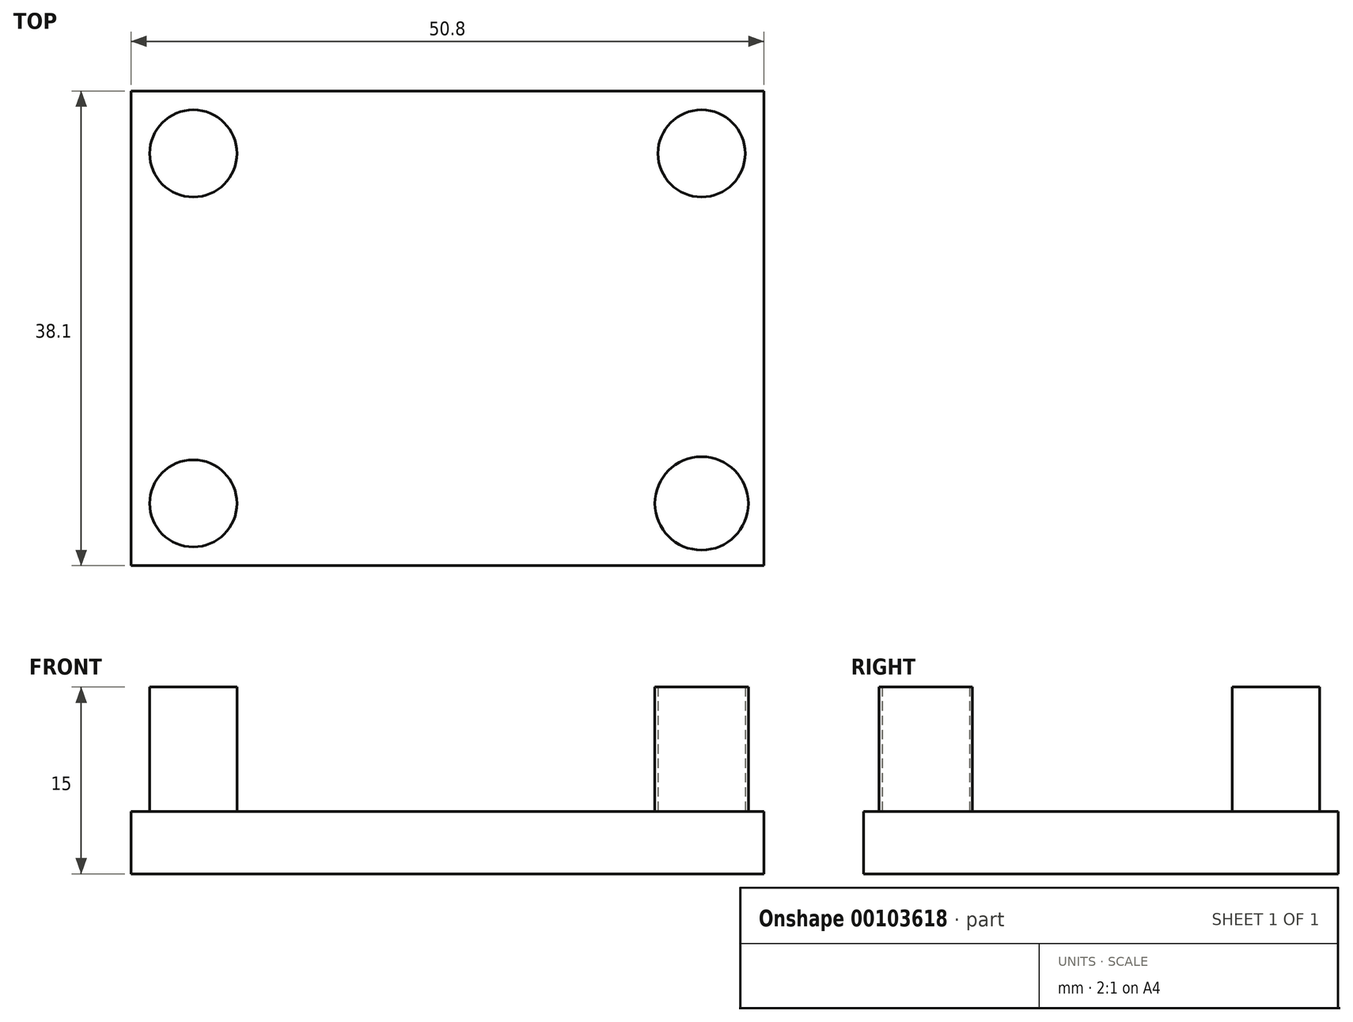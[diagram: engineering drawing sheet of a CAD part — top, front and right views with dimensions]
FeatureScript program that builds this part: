
annotation { "Feature Type Name" : "Feature", "Feature Type Description" : "" }
export const myFeature = defineFeature(function(context is Context, id is Id, definition is map)
    precondition{}
    {
        {
            var Q0;
            Q0=qCreatedBy(makeId("Top.planeOp"),FACE);
            var sketch = newSketch(context, id + "F0", { "sketchPlane" : qUnion([Q0])});
            skLineSegment(sketch, "E0.bottom", {"start": v(-32.92, 10.92) * mm, "end": v(17.88, 10.92) * mm});
            skLineSegment(sketch, "E0.top", {"start": v(-32.92, -27.18) * mm, "end": v(17.88, -27.18) * mm});
            skLineSegment(sketch, "E0.left", {"start": v(-32.92, 10.92) * mm, "end": v(-32.92, -27.18) * mm});
            skLineSegment(sketch, "E0.right", {"start": v(17.88, 10.92) * mm, "end": v(17.88, -27.18) * mm});
            skSolve(sketch);
        }
        {
            var Q0;
            Q0=makeQuery(id+"F0.imprint","IMPRINT",FACE,{"disambiguationData":[TD([[makeQuery(id+"F0.imprint","IMPRINT",EDGE,{"derivedFrom":sQuery(id+"F0.wireOp",EDGE,"E0.bottom")}),-1.0]])]});
            extrude(context, id + "F1", {"entities" : qUnion([Q0]), "depth" : 5 * mm});
        }
        {
            var Q0;
            Q0=makeQuery(id+"F1.opExtrude","CAP_FACE",FACE,{"disambiguationData":[OSD([sQuery(id+"F0.wireOp",EDGE,"E0.bottom"),sQuery(id+"F0.wireOp",EDGE,"E0.top"),sQuery(id+"F0.wireOp",EDGE,"E0.left"),sQuery(id+"F0.wireOp",EDGE,"E0.right")])],"isStart":false});
            var sketch = newSketch(context, id + "F2", { "sketchPlane" : qUnion([Q0])});
            skPoint(sketch, "E1", {"position": v(-27.92, -22.18) * mm});
            skCircle(sketch, "E2", {"center": v(-27.92, -22.18) * mm, "radius": 3.5 * mm});
            skPoint(sketch, "E3", {"position": v(-27.92, 5.92) * mm});
            skCircle(sketch, "E4", {"center": v(-27.92, 5.92) * mm, "radius": 3.5 * mm});
            skPoint(sketch, "E5", {"position": v(12.88, 5.92) * mm});
            skCircle(sketch, "E6", {"center": v(12.88, 5.92) * mm, "radius": 3.5 * mm});
            skPoint(sketch, "E7", {"position": v(12.88, -22.18) * mm});
            skCircle(sketch, "E8", {"center": v(12.88, -22.18) * mm, "radius": 3.75 * mm});
            skSolve(sketch);
        }
        {
            var Q0;
            Q0=makeQuery(id+"F2.imprint","IMPRINT",FACE,{"disambiguationData":[TD([[makeQuery(id+"F2.imprint","IMPRINT",EDGE,{"derivedFrom":sQuery(id+"F2.wireOp",EDGE,"E2")}),1.0]])]});
            var Q1;
            Q1=makeQuery(id+"F2.imprint","IMPRINT",FACE,{"disambiguationData":[TD([[makeQuery(id+"F2.imprint","IMPRINT",EDGE,{"derivedFrom":sQuery(id+"F2.wireOp",EDGE,"E6")}),1.0]])]});
            var Q2;
            Q2=makeQuery(id+"F2.imprint","IMPRINT",FACE,{"disambiguationData":[TD([[makeQuery(id+"F2.imprint","IMPRINT",EDGE,{"derivedFrom":sQuery(id+"F2.wireOp",EDGE,"E8")}),1.0]])]});
            var Q3;
            Q3=makeQuery(id+"F2.imprint","IMPRINT",FACE,{"disambiguationData":[TD([[makeQuery(id+"F2.imprint","IMPRINT",EDGE,{"derivedFrom":sQuery(id+"F2.wireOp",EDGE,"E4")}),1.0]])]});
            extrude(context, id + "F3", {"entities" : qUnion([Q0, Q1, Q2, Q3]), "operationType" : NewBodyOperationType.ADD, "depth" : 10 * mm});
        }
    });
